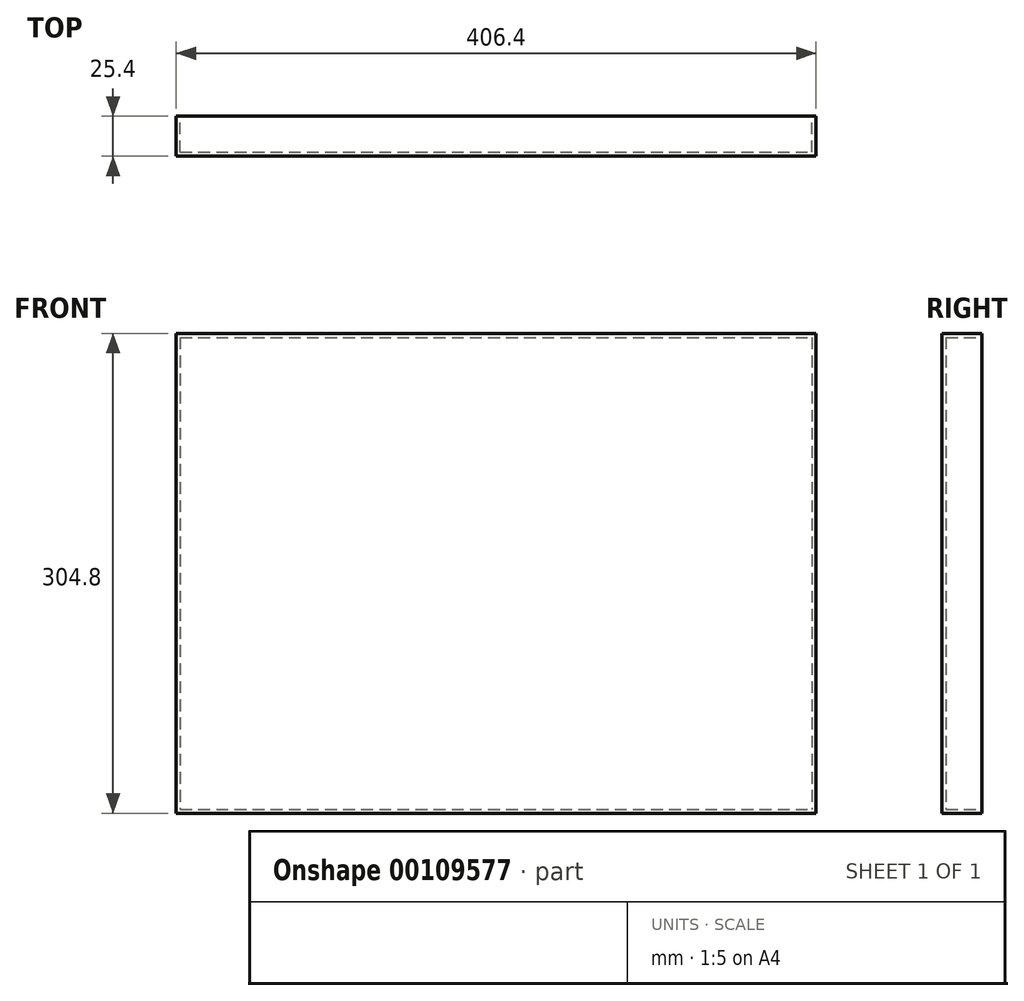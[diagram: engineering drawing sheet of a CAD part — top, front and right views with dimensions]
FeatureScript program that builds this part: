
annotation { "Feature Type Name" : "Feature", "Feature Type Description" : "" }
export const myFeature = defineFeature(function(context is Context, id is Id, definition is map)
    precondition{}
    {
        {
            var Q0;
            Q0=qCreatedBy(makeId("Front.planeOp"),FACE);
            var sketch = newSketch(context, id + "F0", { "sketchPlane" : qUnion([Q0])});
            skLineSegment(sketch, "E0.bottom", {"start": v(-203.2, 150.08) * mm, "end": v(203.2, 150.08) * mm});
            skLineSegment(sketch, "E0.top", {"start": v(-203.2, -154.72) * mm, "end": v(203.2, -154.72) * mm});
            skLineSegment(sketch, "E0.left", {"start": v(-203.2, 150.08) * mm, "end": v(-203.2, -154.72) * mm});
            skLineSegment(sketch, "E0.right", {"start": v(203.2, 150.08) * mm, "end": v(203.2, -154.72) * mm});
            skPoint(sketch, "E0.middle", {"position": v(0, -2.32) * mm});
            skSolve(sketch);
        }
        {
            var Q0;
            Q0 = qSketchRegion(id + "F0", true);
            extrude(context, id + "F1", {"entities" : qUnion([Q0]), "depth" : 25.4 * mm});
        }
        {
            var Q0;
            Q0=makeQuery(id+"F1.opExtrude","CAP_FACE",FACE,{"disambiguationData":[OSD([sQuery(id+"F0.wireOp",EDGE,"E0.bottom"),sQuery(id+"F0.wireOp",EDGE,"E0.top"),sQuery(id+"F0.wireOp",EDGE,"E0.left"),sQuery(id+"F0.wireOp",EDGE,"E0.right")])],"isStart":true});
            shell(context, id + "F2", {"entities" : qUnion([Q0]), "thickness" : 2.54 * mm});
        }
    });
